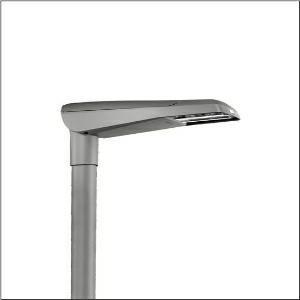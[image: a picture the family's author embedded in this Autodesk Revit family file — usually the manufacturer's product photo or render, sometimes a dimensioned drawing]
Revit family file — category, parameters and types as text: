
# Revit family: streetlight_sl_11_iq_micro___st1_0a_5xc1mc1f08ce_d524
name_source: partatom
category: Lighting Fixtures
units: mm (PartAtom-declared; Revit-internal decimal feet)

## family parameters
Cut with Voids When Loaded = No
Host = Face
Light Source = No
Part Type = Normal
Room Calculation Point = No
Round Connector Dimension = Use Diameter
Shared = No

## types (1)
- --- (1 x LED, 1550 lm, 14 W, 2200K)
    Apparent Load = 14 VA
    CIE Flux Codes = 33 66 96 100 100
    Color Rendering = 70
    Color Temperature = 2200K
    Default Elevation = 1800 mm
    Description = Streetlight SL 11 iQ micro, mast luminaire, primary light control with 3 zone facetted reflector, of plastic, silver coated, highly specular, primary optical cover: cover, of PMMA, transparent, light distribution: ST1.0a, light emission: direct distribution, primary light characteristic: asymmetric, installation type: post-top, side-entry, lamps: LED, High Power LED, rated values: 1.820lm | 13,8W | 131,9lm/W (begin service life); end service life: 1.820lm | 14W; at 50% lumin. flux: 910lm | 7,5W | 121,3lm/W, colour temperature: 2200/2700/3000/4000K, colour rendering: CRI > 70, light colour: 722/727/730/740, light setting 1 begin service life: 100% | 1.820lm | 13,8W | 131,9lm/W | 3.000K, light setting 1 end service life: 14W, further light settings possible, control: Street-Remote, Auto-Match, Temp-Guard, Lumen-Switch, Night-Set, Smart-Wire, Light-Fading, Desk-Remote (wireless, voltage-free reading and setting of iQ features in the workshop via application-optimized NFC function/RFID function), optimised constant luminous flux control (CLO 2.0), with cable H07RN-F 3x 1.5mm², mains connection: 220..240V, AC, 50/60Hz, connection cable pre-assembled, cable length: 5,5m, luminaire housing, of diecast aluminium, powder-coated, SITECO metallic grey (DB 702S), please order mast flange separately, inclination adjustable without tools: 0°, 5°, 10°, 15° (post-top) | 0°, -5°, -10°, -15° (side-entry), sealing non-destructively replaceable, multi-level sealing system, length: 600mm, width: 174mm, height: 116mm, mast flange for spigot size: 42mm (side-entry): 5XC10008XM4, 60/48mm (side-entry/post-top): 5XC10108XM2, 76/60mm (side-entry/post-top): 5XC10108XM1, equipment: standard, protection rating (complete): IP66, insulation class (complete): insulation class II (safety insulation), certification: CE, ENEC, ENEC+, VDE, impact resistance: IK10, permissible operating ambient temperature for outdoor applications: -25..+50°C, standard-compliant lighting for roads and squares, Environmental Product Declaration (EPD) tested and certified by an independent institute, packaging unit: 1 piece

Light Distribution: ST1.0a
    Height = 116 mm
    Lamp = 1 x LED
    Lamp Light Flux = 1550 lm
    Lamp Power = 14 W
    Lamp count = 1
    Length = 600 mm
    Luminous efficacy = 111 lm/W
    Manufacturer = Siteco
    ModVariant = No
    Model = 5XC1MC1F08CE
    Number of Poles = 1
    OnlyDefault = Yes
    Power Factor = 1
    Product Name = Streetlight SL 11 iQ micro | ST1.0a
    Product group = mast luminaire | pylon top
    ProductGroupID = 6100
    Protection Class = Protection class II
    Protection Degree = IP 66
    RLX_Detail_Level = 1
    RLX_Emergency_Light_Flux = 0 lm
    RLX_Emergency_Type = 0
    RLX_Emergency_Type_DB = No
    RlxData = <blob elided: 58049 chars, md5=b67349f3>
    Socket = socket
    Standby Power = 0 W
    System Light Flux = 1550 lm
    System Power = 14 W
    Type Comments = individual setting: luminous flux: 100 % | dim-lin: 254 | 369 mA
    Type Image = l_1006566.jpg
    URL = http://relux.com
    VarID = @adj_042535
    Voltage = 0 V
    Weight = 0.00 kg
    Width = 174 mm

## geometry (parser evidence)
native form markers: Blend x4, Sweep x10
no freeform markers — native parametric forms only
